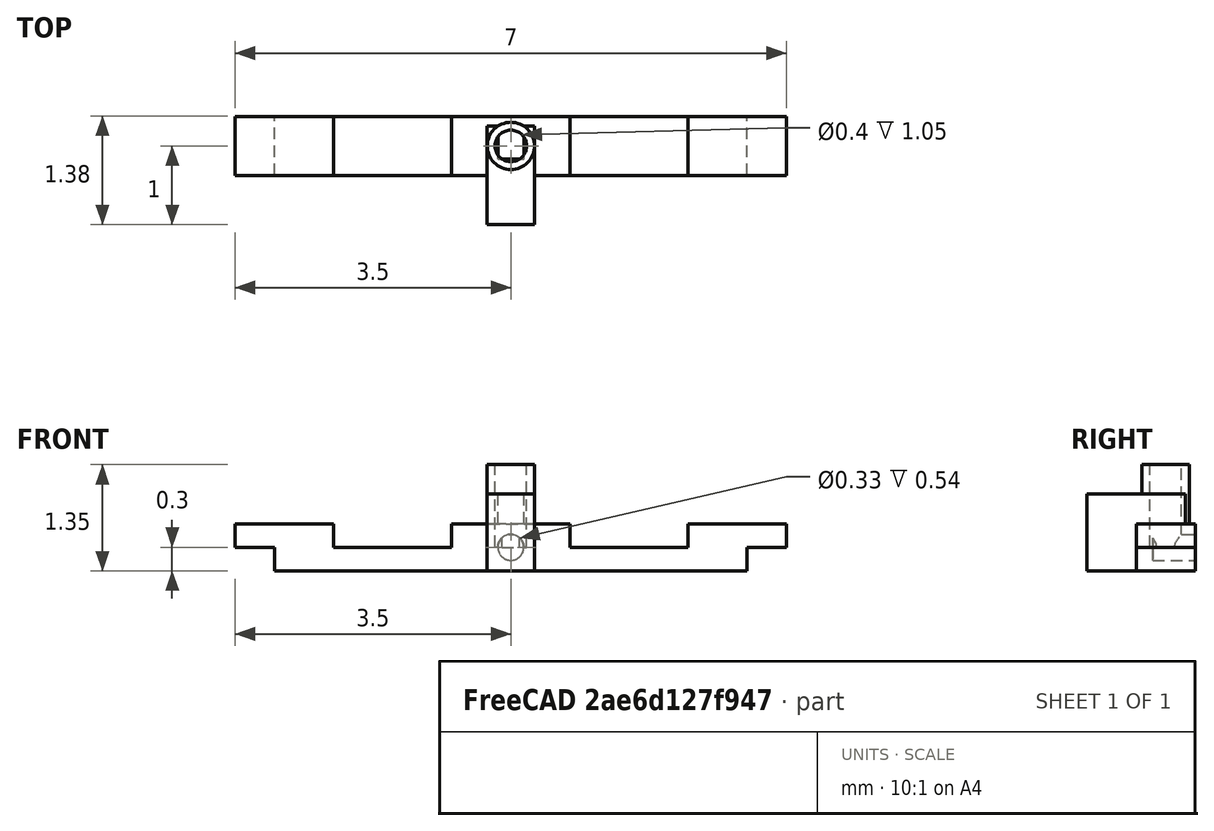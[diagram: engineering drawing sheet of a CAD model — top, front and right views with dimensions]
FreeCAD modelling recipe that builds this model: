
FCSTD DOCUMENT  (FreeCAD 0.17R13509 (Git))
Label: bowtie_4
License: All rights reserved
LicenseURL: http://en.wikipedia.org/wiki/All_rights_reserved
objects: Part::Box×6, Part::Cylinder×3, Part::MultiFuse×3, Spreadsheet::Sheet×1, Part::Cut×1
note: 13 computed .brp shape members not serialized (recipe doc carries the construction recipe); baked Part::Feature solids carry a one-line shape summary decoded from their .brp

FEATURE [Part::Cylinder] Cylinder138  label="BowTieInjectorWire"
  Angle = 360
  AttacherType = Attacher::AttachEngine3D
  Height = 14
  Placement = pos=(0,-0.165,0) rot=(-1,0,0;1.5708rad)
  Radius = 0.165
  expr: Placement.Base.y = -Sizes.NOZZLE_ID / 2
  expr: Radius = 0.33000000000000002 / 2
FEATURE [Part::Cylinder] Cylinder136  label="BowTieNozzle"
  Angle = 360
  AttacherType = Attacher::AttachEngine3D
  Height = 9
  Radius = 0.2
FEATURE [Part::Box] Box  label="Strip"
  AttacherType = Attacher::AttachEngine3D
  Height = 0.6
  Length = 7
  Placement = pos=(-3.5,-0.375,-0.3) rot=(0,0,1;0rad)
  Width = 0.75
  expr: Width = Sizes.STRIP_WIDTH
  expr: Placement.Base.y = -Sizes.STRIP_WIDTH / 2
  expr: Length = Sizes.STRIP_LENGTH
  expr: Placement.Base.x = -Sizes.STRIP_LENGTH / 2
  expr: Height = Sizes.STRIP_HEIGHT
  expr: Placement.Base.z = -Sizes.STRIP_HEIGHT / 2
FEATURE [Spreadsheet::Sheet] Spreadsheet  label="Sizes"
  cells = A1=Strip height; B1(STRIP_HEIGHT)=0.59999999999999998; A2=Strip length; B2(STRIP_LENGTH)=7; A3=strip width; B3(STRIP_WIDTH)=0.75; A4=Injection width; B4(INJECTION_WIDTH)=1.5; A5=Injection length; B5(INJECTION_LENGTH)=1.5; A6=Mounting hole ID; B6(MOUNTING_ID)=2.8439999999999999; A7=Nozzle ID; B7(NOZZLE_ID)=0.33000000000000002; A8=Nozzle OD; B8(NOZZLE_OD)=0.59999999999999998; A9=Mounting hole OD; B9(MOUNTING_OD)=5; A10=Nozzle height; B10(NOZZLE_HEIGHT)=0.75; A11=Mounting hole height; B11(MOUNTING_HEIGHT)=1
FEATURE [Part::Cylinder] Cylinder140  label="Nozzle_OD"
  Angle = 360
  AttacherType = Attacher::AttachEngine3D
  Height = 0.75
  Placement = pos=(0,0,0.3) rot=(0,0,1;0rad)
  Radius = 0.3
  expr: Placement.Base.z = Sizes.STRIP_HEIGHT / 2
  expr: Height = Sizes.NOZZLE_HEIGHT
  expr: Radius = Sizes.NOZZLE_OD / 2
FEATURE [Part::Box] Box001  label="Cube"
  AttacherType = Attacher::AttachEngine3D
  Height = 2
  Length = 1
  Placement = pos=(3,-1,-2) rot=(0,0,1;0rad)
  Width = 2
FEATURE [Part::Box] Box002  label="Cube001"
  AttacherType = Attacher::AttachEngine3D
  Height = 2
  Length = 1
  Placement = pos=(-4,-1,-2) rot=(0,0,1;0rad)
  Width = 2
FEATURE [Part::MultiFuse] Fusion
  Shapes = -> [Box,Cylinder140]
FEATURE [Part::Box] Box003  label="Cube002"
  AttacherType = Attacher::AttachEngine3D
  Height = 0.975
  Length = 0.6
  Placement = pos=(-0.3,-1,-0.3) rot=(0,0,1;0rad)
  Width = 1.25
  expr: Placement.Base.z = -Sizes.STRIP_HEIGHT / 2
  expr: Height = Sizes.STRIP_HEIGHT + Sizes.NOZZLE_HEIGHT / 2
  expr: Width = Sizes.STRIP_WIDTH + 0.5
  expr: Length = Sizes.NOZZLE_OD
FEATURE [Part::Box] Box004  label="Cube003"
  AttacherType = Attacher::AttachEngine3D
  Height = 1
  Length = 1.5
  Placement = pos=(0.75,-1,0) rot=(0,0,1;0rad)
  Width = 2
FEATURE [Part::Box] Box005  label="Cube004"
  AttacherType = Attacher::AttachEngine3D
  Height = 1
  Length = 1.5
  Placement = pos=(-2.25,-1,0) rot=(0,0,1;0rad)
  Width = 2
FEATURE [Part::MultiFuse] Fusion001
  Shapes = -> [Cylinder138,Cylinder136,Box001,Box002,Box004,Box005]
FEATURE [Part::MultiFuse] Fusion002
  Shapes = -> [Fusion,Box003]
FEATURE [Part::Cut] Cut
  Base = -> Fusion002
  Tool = -> Fusion001
